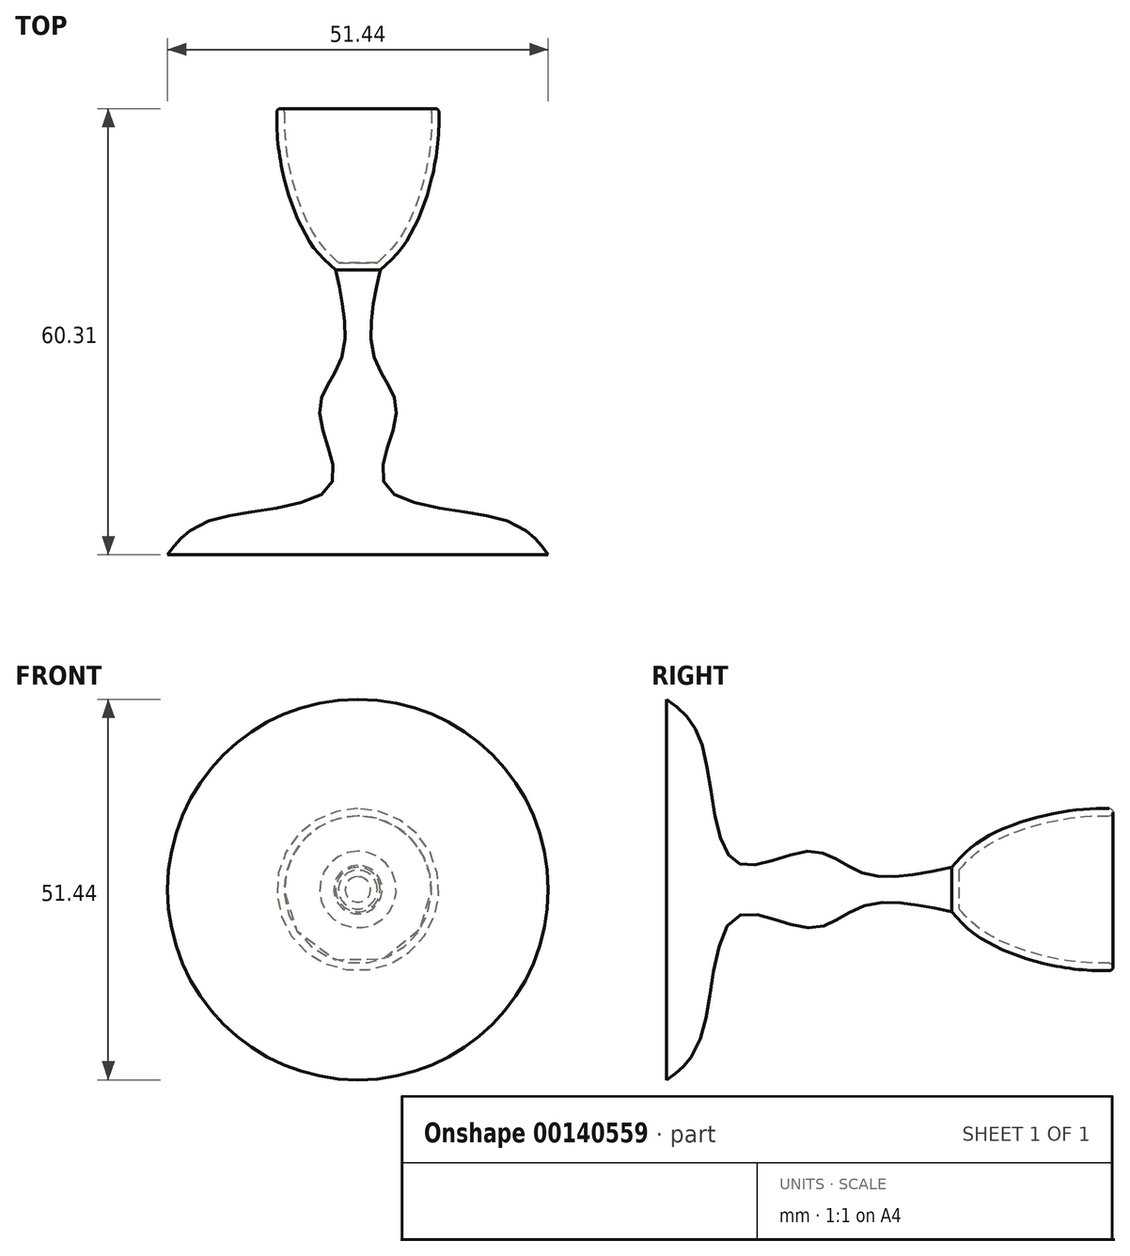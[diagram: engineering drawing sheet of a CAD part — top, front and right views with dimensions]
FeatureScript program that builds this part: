
annotation { "Feature Type Name" : "Feature", "Feature Type Description" : "" }
export const myFeature = defineFeature(function(context is Context, id is Id, definition is map)
    precondition{}
    {
        {
            var Q0;
            Q0=qCreatedBy(makeId("Top.planeOp"),FACE);
            var sketch = newSketch(context, id + "F0", { "sketchPlane" : qUnion([Q0])});
            skLineSegment(sketch, "E0", {"start": v(0, 0) * mm, "end": v(-3, 0) * mm});
            skLineSegment(sketch, "E1", {"start": v(0, 8.3) * mm, "end": v(0, 0) * mm});
            skFitSpline(sketch, "E2", {"points": [v(-3, 0) * mm, v(-6.5, 3.75) * mm, v(-9.46, 10.5) * mm, v(-10.81, 17.24) * mm, v(-10.95, 21.82) * mm], "startDerivative": vector(-15.82, 14.3) * mm, "endDerivative": vector(0.17, 19.93) * mm});
            skLineSegment(sketch, "E3", {"start": v(-10.95, 21.82) * mm, "end": v(0, 21.82) * mm});
            skLineSegment(sketch, "E4", {"start": v(0, 21.82) * mm, "end": v(0, 8.3) * mm});
            skSolve(sketch);
        }
        {
            var Q0;
            Q0=makeQuery(id+"F0.imprint","IMPRINT",FACE,{"disambiguationData":[TD([[makeQuery(id+"F0.imprint","IMPRINT",EDGE,{"derivedFrom":sQuery(id+"F0.wireOp",EDGE,"E0")}),-1.0]])]});
            var Q1;
            Q1=sQuery(id+"F0.wireOp",EDGE,"E1");
            revolve(context, id + "F1", {"entities" : qUnion([Q0]), "axis" : qUnion([Q1]), "revolveType" : RevolveType.FULL});
        }
        {
            var Q0;
            Q0=makeQuery(id+"F1.opRevolve","SWEPT_FACE",FACE,{"disambiguationData":[OSD([sQuery(id+"F0.wireOp",EDGE,"E3")])]});
            shell(context, id + "F2", {"entities" : qUnion([Q0]), "thickness" : 1 * mm});
        }
        {
            var Q0;
            Q0=makeQuery(id+"F1.opRevolve","SWEPT_EDGE",EDGE,{"disambiguationData":[OSD([sQuery(id+"F0.wireOp",EDGE,"E2"),sQuery(id+"F0.wireOp",EDGE,"E3")])]});
            var Q1;
            Q1=makeQuery(id+"F2.opShell","OFFSET_EDGE",EDGE,{"disambiguationData":[OSD([sQuery(id+"F0.wireOp",EDGE,"E2"),sQuery(id+"F0.wireOp",EDGE,"E3")])]});
            fillet(context, id + "F3", {"entities" : qUnion([Q0, Q1]), "radius" : .5 * mm, "tangentPropagation" : true, "allowEdgeOverflow" : false});
        }
        {
            var Q0;
            Q0=qCreatedBy(makeId("Top.planeOp"),FACE);
            var sketch = newSketch(context, id + "F4", { "sketchPlane" : qUnion([Q0])});
            skLineSegment(sketch, "E5.0", {"start": v(-3, 0) * mm, "end": v(3, 0) * mm});
            skLineSegment(sketch, "E6", {"start": v(0, 0) * mm, "end": v(0, -38.49) * mm});
            skLineSegment(sketch, "E7", {"start": v(0, -38.49) * mm, "end": v(25.72, -38.49) * mm});
            skFitSpline(sketch, "E8", {"points": [v(3, 0) * mm, v(2.2, -11.8) * mm, v(5.18, -19.08) * mm, v(3.73, -29.19) * mm, v(19.82, -33.8) * mm, v(25.72, -38.49) * mm], "startDerivative": vector(-13.22, -61.14) * mm, "endDerivative": vector(23.33, -32.3) * mm});
            skSolve(sketch);
        }
        {
            var Q0;
            {var subQ2=sQuery(id+"F4.wireOp",EDGE,"E6");Q0=makeQuery(id+"F4.imprint","IMPRINT",FACE,{"disambiguationData":[TD([[makeQuery(id+"F4.imprint","IMPRINT",EDGE,{"derivedFrom":subQ2}),1.0]])]});}
            var Q1;
            Q1=sQuery(id+"F4.wireOp",EDGE,"E6");
            revolve(context, id + "F5", {"entities" : qUnion([Q0]), "axis" : qUnion([Q1]), "revolveType" : RevolveType.FULL});
        }
    });
